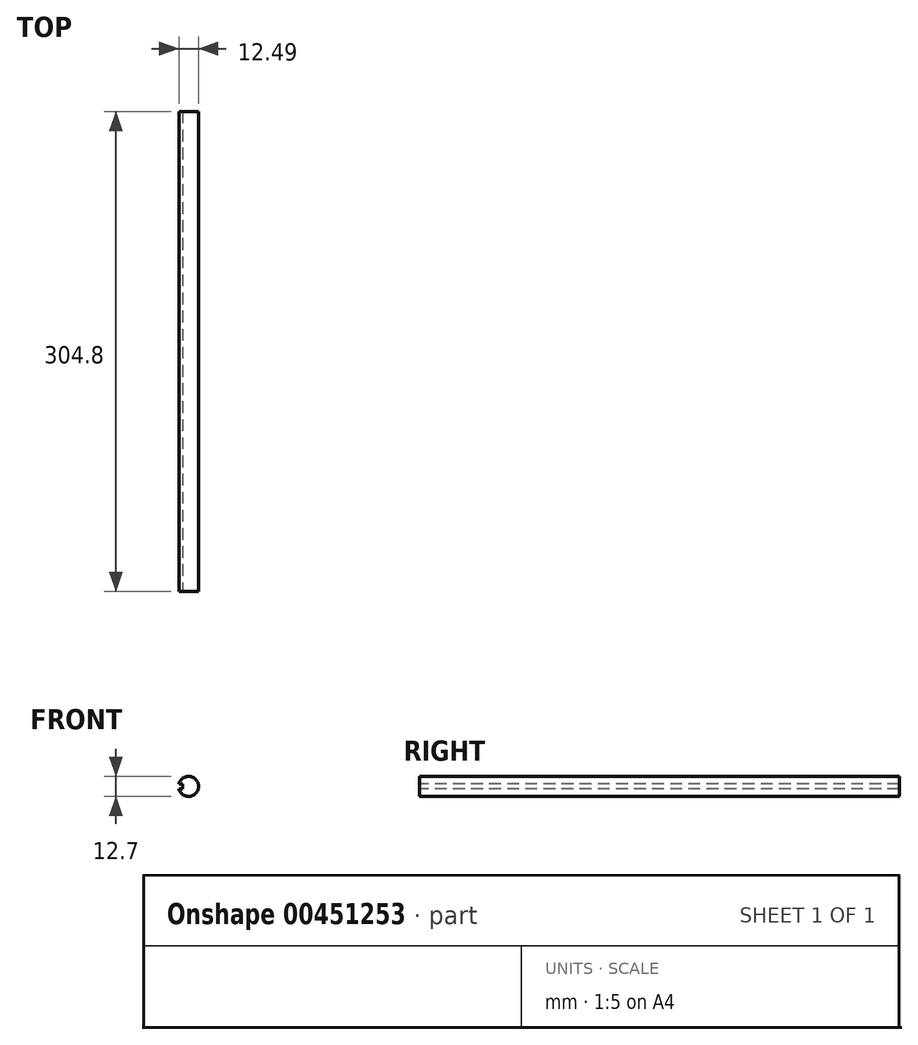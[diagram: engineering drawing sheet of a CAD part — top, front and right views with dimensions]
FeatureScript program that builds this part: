
annotation { "Feature Type Name" : "Feature", "Feature Type Description" : "" }
export const myFeature = defineFeature(function(context is Context, id is Id, definition is map)
    precondition{}
    {
        {
            var Q0;
            Q0=qCreatedBy(makeId("Front.planeOp"),FACE);
            var sketch = newSketch(context, id + "F0", { "sketchPlane" : qUnion([Q0])});
            skArc(sketch, "E0", {"start": v(-6.14, -1.64) * mm, "mid": v(6.35, 0) * mm, "end": v(-6.14, 1.64) * mm});
            skLineSegment(sketch, "E1", {"start": v(-6.14, 1.64) * mm, "end": v(-3.81, 1.64) * mm});
            skLineSegment(sketch, "E2", {"start": v(-6.14, -1.64) * mm, "end": v(-3.81, -1.64) * mm});
            skLineSegment(sketch, "E3", {"start": v(-3.81, 1.64) * mm, "end": v(-3.81, -1.64) * mm});
            skSolve(sketch);
        }
        {
            var Q0;
            Q0 = qSketchRegion(id + "F0", true);
            extrude(context, id + "F1", {"entities" : qUnion([Q0]), "oppositeDirection" : true, "depth" : 304.8 * mm});
        }
    });
